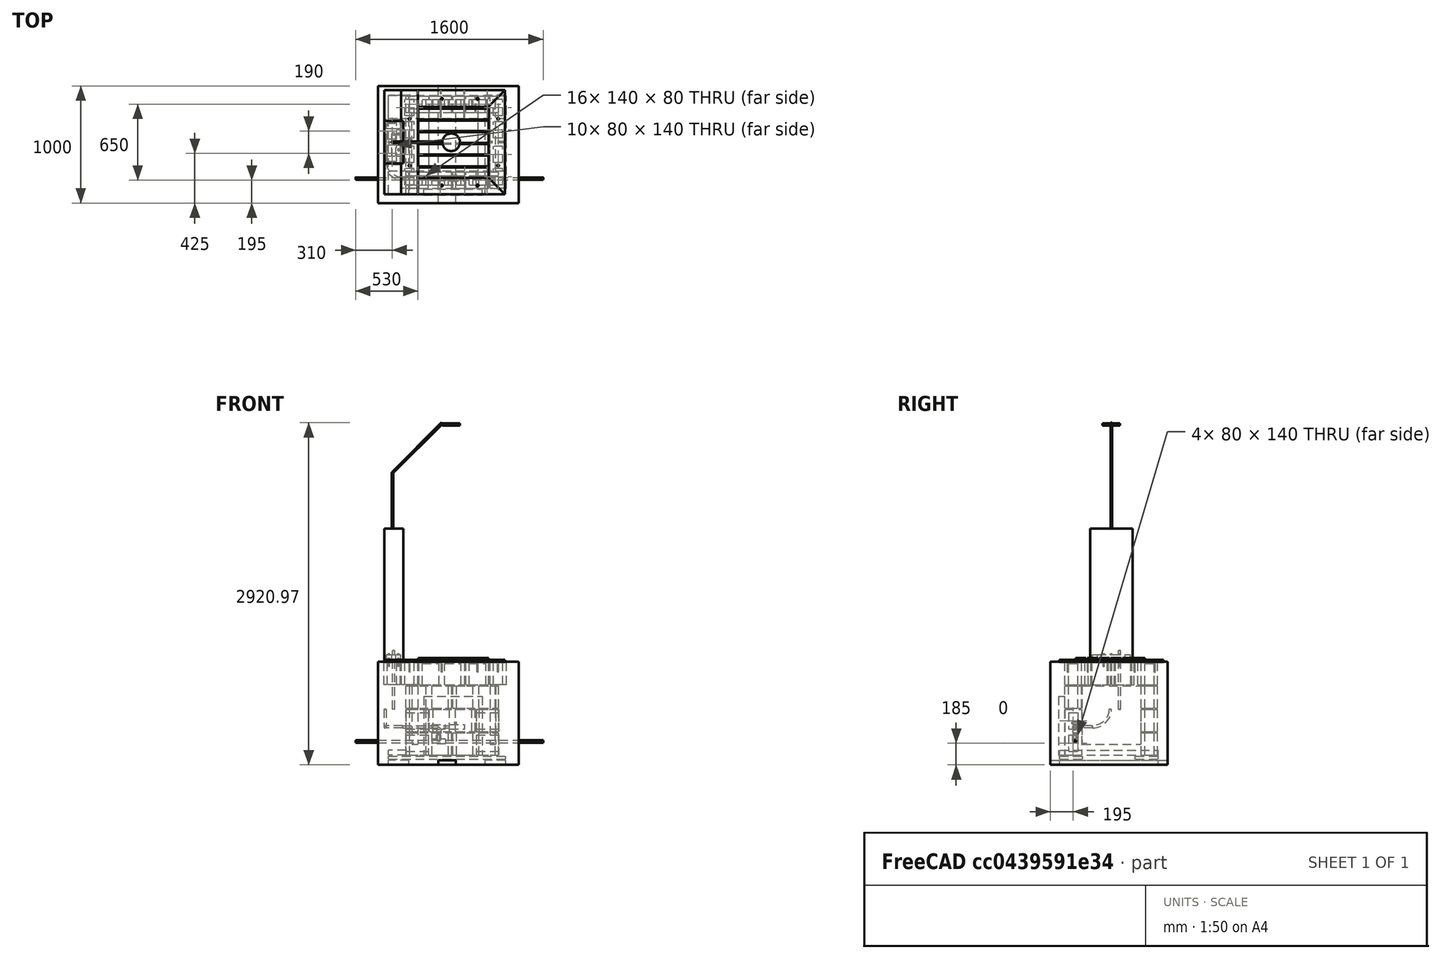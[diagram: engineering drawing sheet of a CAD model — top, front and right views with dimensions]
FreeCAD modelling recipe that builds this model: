
FCSTD DOCUMENT  (FreeCAD 0.18.3R)
Label: douchesokkel v2
License: All rights reserved
LicenseURL: http://en.wikipedia.org/wiki/All_rights_reserved
objects: Part::Box×89, Part::Cylinder×34, Part::MultiFuse×24, Part::Cut×20, Part::Compound×13, Part::Chamfer×3, Part::Torus×2
note: 185 computed .brp shape members not serialized (recipe doc carries the construction recipe); baked Part::Feature solids carry a one-line shape summary decoded from their .brp

FEATURE [Part::Box] Box  label="douchesokkel"
  AttacherType = Attacher::AttachEngine3D
  Height = 1120
  Length = 160
  Placement = pos=(45,10,21) rot=(0,0,1;0rad)
  Width = 360
FEATURE [Part::Cylinder] Cylinder  label="douchebuis"
  Angle = 360
  AttacherType = Attacher::AttachEngine3D
  Height = 480
  Placement = pos=(115,190,1141) rot=(0,0,1;0rad)
  Radius = 7
FEATURE [Part::Cylinder] Cylinder001  label="douchebuis001"
  Angle = 360
  AttacherType = Attacher::AttachEngine3D
  Height = 594
  Placement = pos=(115,190,1621) rot=(0,1,0;0.785398rad)
  Radius = 7
FEATURE [Part::Cylinder] Cylinder002  label="douchekop"
  Angle = 360
  AttacherType = Attacher::AttachEngine3D
  Height = 20
  Placement = pos=(615,190,2021) rot=(0,0,1;0rad)
  Radius = 75
FEATURE [Part::Box] Box001  label="put"
  AttacherType = Attacher::AttachEngine3D
  Height = 880
  Length = 1200
  Placement = pos=(-10,-330,-875) rot=(0,0,1;0rad)
  Width = 1000
FEATURE [Part::Cylinder] Cylinder003  label="Cylinder"
  Angle = 360
  AttacherType = Attacher::AttachEngine3D
  Height = 116
  Radius = 20
FEATURE [Part::Cylinder] Cylinder004  label="Cylinder001"
  Angle = 360
  AttacherType = Attacher::AttachEngine3D
  Height = 55
  Placement = pos=(0,0,58) rot=(0,1,0;1.5708rad)
  Radius = 20
FEATURE [Part::MultiFuse] Fusion  label="T-stuk"
  Placement = pos=(450,-120,-550) rot=(0,1,0;1.5708rad)
  Shapes = -> [Cylinder004,Cylinder003]
FEATURE [Part::Cylinder] Cylinder005  label="Cylinder002"
  Angle = 360
  AttacherType = Attacher::AttachEngine3D
  Height = 55
  Placement = pos=(0,0,58) rot=(0,1,0;1.5708rad)
  Radius = 20
FEATURE [Part::Cylinder] Cylinder006  label="Cylinder003"
  Angle = 360
  AttacherType = Attacher::AttachEngine3D
  Height = 116
  Radius = 20
FEATURE [Part::MultiFuse] Fusion001  label="T-stuk001"
  Placement = pos=(566,-120,-675) rot=(0,-1,0;1.5708rad)
  Shapes = -> [Cylinder005,Cylinder006]
FEATURE [Part::Cylinder] Cylinder007  label="Cylinder004"
  Angle = 360
  AttacherType = Attacher::AttachEngine3D
  Height = 130
  Placement = pos=(0,0,0) rot=(0,1,0;1.5708rad)
  Radius = 20
FEATURE [Part::Box] Box002  label="Cube"
  AttacherType = Attacher::AttachEngine3D
  Height = 15
  Length = 15
  Placement = pos=(46,-25,25) rot=(0,0,1;0rad)
  Width = 58
FEATURE [Part::Cylinder] Cylinder008  label="tyleen huis-yurt"
  Angle = 360
  AttacherType = Attacher::AttachEngine3D
  Height = 1600
  Placement = pos=(-200,-120,-675) rot=(0,1,0;1.5708rad)
  Radius = 10
FEATURE [Part::MultiFuse] Fusion002  label="kraan"
  Placement = pos=(600,-120,-550) rot=(0,0,1;0rad)
  Shapes = -> [Cylinder007,Box002]
FEATURE [Part::Cylinder] Cylinder009  label="Cylinder006"
  Angle = 360
  AttacherType = Attacher::AttachEngine3D
  Height = 400
  Placement = pos=(200,-100,-550) rot=(0,1,0;1.5708rad)
  Radius = 10
FEATURE [Part::Torus] Torus
  Angle1 = 180
  Angle2 = 180
  Angle3 = 90
  AttacherType = Attacher::AttachEngine3D
  Placement = pos=(200,50,-550) rot=(0,0,1;3.14159rad)
  Radius1 = 150
  Radius2 = 10
FEATURE [Part::Torus] Torus001
  Angle1 = 180
  Angle2 = 180
  Angle3 = 90
  AttacherType = Attacher::AttachEngine3D
  Placement = pos=(50,50,-400) rot=(0,1,0;1.5708rad)
  Radius1 = 150
  Radius2 = 10
FEATURE [Part::Cylinder] Cylinder010  label="Cylinder005"
  Angle = 360
  AttacherType = Attacher::AttachEngine3D
  Height = 500
  Placement = pos=(125,280,-400) rot=(0,0,1;0rad)
  Radius = 10
FEATURE [Part::Compound] Compound  label="tyleen douche"
  Links = -> [Cylinder009,Torus,Torus001,Cylinder010]
  Placement = pos=(0,-20,0) rot=(0,0,1;0rad)
FEATURE [Part::Cylinder] Cylinder011  label="tyleen"
  Angle = 360
  AttacherType = Attacher::AttachEngine3D
  Height = 100
  Placement = pos=(508,-120,-675) rot=(0,1,0;0rad)
  Radius = 10
FEATURE [Part::Box] Box010  label="Cube004"
  AttacherType = Attacher::AttachEngine3D
  Height = 190
  Length = 140
  Placement = pos=(220,30,0) rot=(0,0,1;0rad)
  Width = 80
FEATURE [Part::Box] Box011  label="Cube005"
  AttacherType = Attacher::AttachEngine3D
  Height = 190
  Length = 140
  Placement = pos=(30,30,0) rot=(0,0,1;0rad)
  Width = 80
FEATURE [Part::MultiFuse] Fusion004
  Shapes = -> [Box011,Box010]
FEATURE [Part::Box] Box012  label="Cube006"
  AttacherType = Attacher::AttachEngine3D
  Height = 190
  Length = 390
  Width = 140
FEATURE [Part::Cut] Cut001  label="snelbouwsteen (2x)001"
  Base = -> Box012
  Placement = pos=(230,-205,-400) rot=(0,1,0;1.5708rad)
  Tool = -> Fusion004
FEATURE [Part::Box] Box013  label="dal (5x)001"
  AttacherType = Attacher::AttachEngine3D
  Height = 50
  Length = 500
  Placement = pos=(280,-60,-200) rot=(0,1,0;1.5708rad)
  Width = 500
FEATURE [Part::Box] Box014  label="dal (5x)002"
  AttacherType = Attacher::AttachEngine3D
  Height = 50
  Length = 500
  Placement = pos=(945,-60,-200) rot=(0,1,0;1.5708rad)
  Width = 500
FEATURE [Part::Box] Box015  label="dal (5x)003"
  AttacherType = Attacher::AttachEngine3D
  Height = 50
  Length = 500
  Placement = pos=(380,-260,-290) rot=(-1,0,0;1.5708rad)
  Width = 500
FEATURE [Part::Box] Box017  label="Cube007"
  AttacherType = Attacher::AttachEngine3D
  Height = 190
  Length = 140
  Placement = pos=(220,30,0) rot=(0,0,1;0rad)
  Width = 80
FEATURE [Part::Box] Box018  label="Cube008"
  AttacherType = Attacher::AttachEngine3D
  Height = 190
  Length = 140
  Placement = pos=(30,30,0) rot=(0,0,1;0rad)
  Width = 80
FEATURE [Part::MultiFuse] Fusion005
  Shapes = -> [Box018,Box017]
FEATURE [Part::Box] Box019  label="Cube009"
  AttacherType = Attacher::AttachEngine3D
  Height = 190
  Length = 390
  Width = 140
FEATURE [Part::Cut] Cut002  label="snelbouwsteen (2x)002"
  Base = -> Box019
  Placement = pos=(230,-205,-390) rot=(0,1,0;0rad)
  Tool = -> Fusion005
FEATURE [Part::Box] Box020  label="Cube010"
  AttacherType = Attacher::AttachEngine3D
  Height = 190
  Length = 140
  Placement = pos=(220,30,0) rot=(0,0,1;0rad)
  Width = 80
FEATURE [Part::Box] Box021  label="Cube011"
  AttacherType = Attacher::AttachEngine3D
  Height = 190
  Length = 140
  Placement = pos=(30,30,0) rot=(0,0,1;0rad)
  Width = 80
FEATURE [Part::MultiFuse] Fusion006
  Shapes = -> [Box021,Box020]
FEATURE [Part::Box] Box022  label="Cube012"
  AttacherType = Attacher::AttachEngine3D
  Height = 190
  Length = 390
  Width = 140
FEATURE [Part::Cut] Cut003  label="snelbouwsteen (2x)003"
  Base = -> Box022
  Placement = pos=(230,445,-790) rot=(0,1,0;0rad)
  Tool = -> Fusion006
FEATURE [Part::Box] Box023  label="Cube013"
  AttacherType = Attacher::AttachEngine3D
  Height = 190
  Length = 140
  Placement = pos=(30,30,0) rot=(0,0,1;0rad)
  Width = 80
FEATURE [Part::Box] Box024  label="Cube014"
  AttacherType = Attacher::AttachEngine3D
  Height = 190
  Length = 390
  Width = 140
FEATURE [Part::Box] Box025  label="Cube015"
  AttacherType = Attacher::AttachEngine3D
  Height = 190
  Length = 140
  Placement = pos=(220,30,0) rot=(0,0,1;0rad)
  Width = 80
FEATURE [Part::MultiFuse] Fusion007
  Shapes = -> [Box023,Box025]
FEATURE [Part::Cut] Cut004  label="snelbouwsteen (2x)004"
  Base = -> Box024
  Placement = pos=(230,445,-390) rot=(0,1,0;0rad)
  Tool = -> Fusion007
FEATURE [Part::Box] Box026  label="Cube016"
  AttacherType = Attacher::AttachEngine3D
  Height = 190
  Length = 140
  Placement = pos=(220,30,0) rot=(0,0,1;0rad)
  Width = 80
FEATURE [Part::Box] Box027  label="Cube017"
  AttacherType = Attacher::AttachEngine3D
  Height = 190
  Length = 140
  Placement = pos=(30,30,0) rot=(0,0,1;0rad)
  Width = 80
FEATURE [Part::MultiFuse] Fusion008
  Shapes = -> [Box027,Box026]
FEATURE [Part::Box] Box028  label="Cube018"
  AttacherType = Attacher::AttachEngine3D
  Height = 190
  Length = 390
  Width = 140
FEATURE [Part::Cut] Cut005  label="snelbouwsteen (2x)005"
  Base = -> Box028
  Placement = pos=(830,-205,-400) rot=(0,1,0;1.5708rad)
  Tool = -> Fusion008
FEATURE [Part::Box] Box029  label="Cube019"
  AttacherType = Attacher::AttachEngine3D
  Height = 190
  Length = 140
  Placement = pos=(30,30,0) rot=(0,0,1;0rad)
  Width = 80
FEATURE [Part::Box] Box030  label="Cube020"
  AttacherType = Attacher::AttachEngine3D
  Height = 190
  Length = 390
  Width = 140
FEATURE [Part::Box] Box031  label="Cube021"
  AttacherType = Attacher::AttachEngine3D
  Height = 190
  Length = 140
  Placement = pos=(220,30,0) rot=(0,0,1;0rad)
  Width = 80
FEATURE [Part::MultiFuse] Fusion009
  Shapes = -> [Box029,Box031]
FEATURE [Part::Cut] Cut006  label="snelbouwsteen (2x)006"
  Base = -> Box030
  Placement = pos=(630,-205,-390) rot=(0,1,0;0rad)
  Tool = -> Fusion009
FEATURE [Part::Box] Box032  label="Cube022"
  AttacherType = Attacher::AttachEngine3D
  Height = 190
  Length = 140
  Placement = pos=(30,30,0) rot=(0,0,1;0rad)
  Width = 80
FEATURE [Part::Box] Box033  label="Cube023"
  AttacherType = Attacher::AttachEngine3D
  Height = 190
  Length = 390
  Width = 140
FEATURE [Part::Box] Box034  label="Cube024"
  AttacherType = Attacher::AttachEngine3D
  Height = 190
  Length = 140
  Placement = pos=(220,30,0) rot=(0,0,1;0rad)
  Width = 80
FEATURE [Part::MultiFuse] Fusion010
  Shapes = -> [Box032,Box034]
FEATURE [Part::Cut] Cut007  label="snelbouwsteen (2x)007"
  Base = -> Box033
  Placement = pos=(630,445,-390) rot=(0,1,0;0rad)
  Tool = -> Fusion010
FEATURE [Part::Box] Box035  label="Cube025"
  AttacherType = Attacher::AttachEngine3D
  Height = 190
  Length = 140
  Placement = pos=(220,30,0) rot=(0,0,1;0rad)
  Width = 80
FEATURE [Part::Box] Box036  label="Cube026"
  AttacherType = Attacher::AttachEngine3D
  Height = 190
  Length = 140
  Placement = pos=(30,30,0) rot=(0,0,1;0rad)
  Width = 80
FEATURE [Part::MultiFuse] Fusion011
  Shapes = -> [Box036,Box035]
FEATURE [Part::Box] Box037  label="Cube027"
  AttacherType = Attacher::AttachEngine3D
  Height = 190
  Length = 390
  Width = 140
FEATURE [Part::Cut] Cut008  label="snelbouwsteen (2x)008"
  Base = -> Box037
  Placement = pos=(630,445,-790) rot=(0,1,0;0rad)
  Tool = -> Fusion011
FEATURE [Part::Box] Box042  label="boord (5x)001"
  AttacherType = Attacher::AttachEngine3D
  Height = 25
  Length = 1000
  Placement = pos=(80,-250,-825) rot=(0,0,1;0rad)
  Width = 195
FEATURE [Part::Box] Box044  label="boord (5x)002"
  AttacherType = Attacher::AttachEngine3D
  Height = 25
  Length = 1000
  Placement = pos=(80,395,-825) rot=(0,0,1;0rad)
  Width = 195
FEATURE [Part::Box] Box046  label="balk (5x)001"
  AttacherType = Attacher::AttachEngine3D
  Height = 40
  Length = 840
  Placement = pos=(255,-250,-875) rot=(0,0,1;1.5708rad)
  Width = 175
FEATURE [Part::Box] Box047  label="balk (5x)002"
  AttacherType = Attacher::AttachEngine3D
  Height = 40
  Length = 840
  Placement = pos=(1080,-250,-875) rot=(0,0,1;1.5708rad)
  Width = 175
FEATURE [Part::Box] Box048  label="balk (5x)003"
  AttacherType = Attacher::AttachEngine3D
  Height = 40
  Length = 1000
  Placement = pos=(655,-330,-875) rot=(0,0,1;1.5708rad)
  Width = 150
FEATURE [Part::Box] Box052  label="balk (5x)005"
  AttacherType = Attacher::AttachEngine3D
  Height = 40
  Length = 840
  Placement = pos=(230,-250,-790) rot=(0,0,1;1.5708rad)
  Width = 150
FEATURE [Part::Box] Box056  label="Cube028"
  AttacherType = Attacher::AttachEngine3D
  Height = 190
  Length = 140
  Placement = pos=(220,30,0) rot=(0,0,1;0rad)
  Width = 80
FEATURE [Part::Box] Box057  label="Cube029"
  AttacherType = Attacher::AttachEngine3D
  Height = 190
  Length = 140
  Placement = pos=(30,30,0) rot=(0,0,1;0rad)
  Width = 80
FEATURE [Part::MultiFuse] Fusion012
  Shapes = -> [Box057,Box056]
FEATURE [Part::Box] Box058  label="Cube030"
  AttacherType = Attacher::AttachEngine3D
  Height = 190
  Length = 390
  Width = 140
FEATURE [Part::Cut] Cut009  label="snelbouwsteen (2x)009"
  Base = -> Box058
  Placement = pos=(180,-5,-190) rot=(0,0,1;1.5708rad)
  Tool = -> Fusion012
FEATURE [Part::Box] Box076  label="Cube048"
  AttacherType = Attacher::AttachEngine3D
  Height = 19
  Length = 600
  Width = 90
FEATURE [Part::Box] Box077  label="Cube049"
  AttacherType = Attacher::AttachEngine3D
  Height = 19
  Length = 600
  Placement = pos=(0,100,0) rot=(0,0,1;0rad)
  Width = 90
FEATURE [Part::Box] Box078  label="Cube050"
  AttacherType = Attacher::AttachEngine3D
  Height = 19
  Length = 600
  Placement = pos=(0,200,0) rot=(0,0,1;0rad)
  Width = 90
FEATURE [Part::Box] Box079  label="Cube051"
  AttacherType = Attacher::AttachEngine3D
  Height = 19
  Length = 600
  Placement = pos=(0,300,0) rot=(0,0,1;0rad)
  Width = 90
FEATURE [Part::Box] Box080  label="Cube052"
  AttacherType = Attacher::AttachEngine3D
  Height = 19
  Length = 600
  Placement = pos=(0,400,0) rot=(0,0,1;0rad)
  Width = 90
FEATURE [Part::Box] Box081  label="Cube053"
  AttacherType = Attacher::AttachEngine3D
  Height = 19
  Length = 600
  Placement = pos=(0,500,0) rot=(0,0,1;0rad)
  Width = 90
FEATURE [Part::Box] Box082  label="Cube054"
  AttacherType = Attacher::AttachEngine3D
  Height = 19
  Length = 90
  Placement = pos=(0,0,-19) rot=(0,0,1;0rad)
  Width = 600
FEATURE [Part::Box] Box083  label="Cube055"
  AttacherType = Attacher::AttachEngine3D
  Height = 19
  Length = 90
  Placement = pos=(510,0,-19) rot=(0,0,1;0rad)
  Width = 600
FEATURE [Part::MultiFuse] Fusion014  label="tuintegel 60x60"
  Placement = pos=(335,-115,19) rot=(0,0,1;0rad)
  Shapes = -> [Box083,Box077,Box076,Box082,Box079,Box078,Box081,Box080]
FEATURE [Part::Box] Box084  label="Cube056"
  AttacherType = Attacher::AttachEngine3D
  Height = 21
  Length = 743
  Placement = pos=(286,-275,0) rot=(0,0,1;0rad)
  Width = 143
FEATURE [Part::Box] Box085  label="Cube057"
  AttacherType = Attacher::AttachEngine3D
  Height = 21
  Length = 743
  Placement = pos=(286,472,0) rot=(0,0,1;0rad)
  Width = 143
FEATURE [Part::Box] Box086  label="Cube058"
  AttacherType = Attacher::AttachEngine3D
  Height = 21
  Length = 143
  Placement = pos=(143,-275,0) rot=(0,0,1;0rad)
  Width = 890
FEATURE [Part::Box] Box087  label="Cube059"
  AttacherType = Attacher::AttachEngine3D
  Height = 21
  Length = 143
  Placement = pos=(886,-275,0) rot=(0,0,1;0rad)
  Width = 890
FEATURE [Part::Box] Box092  label="Cube064"
  AttacherType = Attacher::AttachEngine3D
  Height = 21
  Length = 143
  Placement = pos=(0,-275,0) rot=(0,0,1;0rad)
  Width = 890
FEATURE [Part::Chamfer] Chamfer
  Base = -> Box084
  Edges = 1 edges r=142.9: [Edge7]
FEATURE [Part::Chamfer] Chamfer001
  Base = -> Box085
  Edges = 1 edges r=142.9: [Edge5]
FEATURE [Part::Chamfer] Chamfer002
  Base = -> Box087
  Edges = 2 edges r=142.9: [Edge1,Edge3]
FEATURE [Part::Compound] Compound002  label="plankenwerk"
  Links = -> [Chamfer002,Chamfer001,Chamfer,Box092,Box086]
  Placement = pos=(45,20,0) rot=(0,0,1;0rad)
FEATURE [Part::Box] Box095  label="Cube067"
  AttacherType = Attacher::AttachEngine3D
  Height = 190
  Length = 140
  Placement = pos=(30,30,0) rot=(0,0,1;0rad)
  Width = 80
FEATURE [Part::Box] Box096  label="Cube068"
  AttacherType = Attacher::AttachEngine3D
  Height = 190
  Length = 390
  Width = 140
FEATURE [Part::Box] Box097  label="Cube069"
  AttacherType = Attacher::AttachEngine3D
  Height = 190
  Length = 140
  Placement = pos=(220,30,0) rot=(0,0,1;0rad)
  Width = 80
FEATURE [Part::MultiFuse] Fusion015
  Shapes = -> [Box095,Box097]
FEATURE [Part::Cut] Cut010  label="snelbouwsteen (2x)010"
  Base = -> Box096
  Placement = pos=(430,445,-590) rot=(0,1,0;0rad)
  Tool = -> Fusion015
FEATURE [Part::Box] Box098  label="Cube070"
  AttacherType = Attacher::AttachEngine3D
  Height = 190
  Length = 140
  Placement = pos=(30,30,0) rot=(0,0,1;0rad)
  Width = 80
FEATURE [Part::Box] Box099  label="Cube071"
  AttacherType = Attacher::AttachEngine3D
  Height = 190
  Length = 140
  Placement = pos=(220,30,0) rot=(0,0,1;0rad)
  Width = 80
FEATURE [Part::MultiFuse] Fusion016
  Shapes = -> [Box098,Box099]
FEATURE [Part::Box] Box100  label="Cube072"
  AttacherType = Attacher::AttachEngine3D
  Height = 190
  Length = 195
  Width = 140
FEATURE [Part::Cut] Cut011  label="halve snelbouwsteen"
  Base = -> Box100
  Placement = pos=(230,445,-590) rot=(0,1,0;0rad)
  Tool = -> Fusion016
FEATURE [Part::Box] Box101  label="Cube073"
  AttacherType = Attacher::AttachEngine3D
  Height = 190
  Length = 140
  Placement = pos=(220,30,0) rot=(0,0,1;0rad)
  Width = 80
FEATURE [Part::Box] Box102  label="Cube074"
  AttacherType = Attacher::AttachEngine3D
  Height = 190
  Length = 140
  Placement = pos=(30,30,0) rot=(0,0,1;0rad)
  Width = 80
FEATURE [Part::MultiFuse] Fusion017
  Shapes = -> [Box102,Box101]
FEATURE [Part::Box] Box103  label="Cube075"
  AttacherType = Attacher::AttachEngine3D
  Height = 190
  Length = 195
  Width = 140
FEATURE [Part::Cut] Cut012  label="halve snelbouwsteen001"
  Base = -> Box103
  Placement = pos=(825,445,-590) rot=(0,1,0;0rad)
  Tool = -> Fusion017
FEATURE [Part::Box] Box104  label="Cube076"
  AttacherType = Attacher::AttachEngine3D
  Height = 180
  Length = 140
  Placement = pos=(30,30,0) rot=(0,0,1;0rad)
  Width = 80
FEATURE [Part::Box] Box105  label="Cube077"
  AttacherType = Attacher::AttachEngine3D
  Height = 180
  Length = 140
  Placement = pos=(220,30,0) rot=(0,0,1;0rad)
  Width = 80
FEATURE [Part::MultiFuse] Fusion018
  Shapes = -> [Box104,Box105]
FEATURE [Part::Box] Box106  label="Cube078"
  AttacherType = Attacher::AttachEngine3D
  Height = 190
  Length = 390
  Width = 140
FEATURE [Part::Cut] Cut013  label="snelbouwsteen (2x)011"
  Base = -> Box106
  Placement = pos=(340,445,-190) rot=(0,1,0;0rad)
  Tool = -> Fusion018
FEATURE [Part::Box] Box107  label="Cube079"
  AttacherType = Attacher::AttachEngine3D
  Height = 190
  Length = 390
  Width = 140
FEATURE [Part::Box] Box108  label="Cube080"
  AttacherType = Attacher::AttachEngine3D
  Height = 180
  Length = 140
  Placement = pos=(220,30,0) rot=(0,0,1;0rad)
  Width = 80
FEATURE [Part::Box] Box109  label="Cube081"
  AttacherType = Attacher::AttachEngine3D
  Height = 180
  Length = 140
  Placement = pos=(30,30,0) rot=(0,0,1;0rad)
  Width = 80
FEATURE [Part::MultiFuse] Fusion019
  Shapes = -> [Box109,Box108]
FEATURE [Part::Cut] Cut014  label="snelbouwsteen (2x)012"
  Base = -> Box107
  Placement = pos=(340,-205,-190) rot=(0,1,0;0rad)
  Tool = -> Fusion019
FEATURE [Part::Box] Box110  label="Cube082"
  AttacherType = Attacher::AttachEngine3D
  Height = 190
  Length = 390
  Width = 140
FEATURE [Part::Box] Box111  label="Cube083"
  AttacherType = Attacher::AttachEngine3D
  Height = 190
  Length = 140
  Placement = pos=(30,30,0) rot=(0,0,1;0rad)
  Width = 80
FEATURE [Part::Box] Box112  label="Cube084"
  AttacherType = Attacher::AttachEngine3D
  Height = 190
  Length = 140
  Placement = pos=(220,30,0) rot=(0,0,1;0rad)
  Width = 80
FEATURE [Part::MultiFuse] Fusion020
  Shapes = -> [Box111,Box112]
FEATURE [Part::Cut] Cut015  label="snelbouwsteen (2x)013"
  Base = -> Box110
  Placement = pos=(330,-205,-190) rot=(0,0,1;1.5708rad)
  Tool = -> Fusion020
FEATURE [Part::Box] Box113  label="Cube085"
  AttacherType = Attacher::AttachEngine3D
  Height = 190
  Length = 140
  Placement = pos=(220,30,0) rot=(0,0,1;0rad)
  Width = 80
FEATURE [Part::Box] Box114  label="Cube086"
  AttacherType = Attacher::AttachEngine3D
  Height = 190
  Length = 140
  Placement = pos=(30,30,0) rot=(0,0,1;0rad)
  Width = 80
FEATURE [Part::MultiFuse] Fusion021
  Shapes = -> [Box114,Box113]
FEATURE [Part::Box] Box115  label="Cube087"
  AttacherType = Attacher::AttachEngine3D
  Height = 190
  Length = 390
  Width = 140
FEATURE [Part::Cut] Cut016  label="snelbouwsteen (2x)014"
  Base = -> Box115
  Placement = pos=(330,195,-190) rot=(0,0,1;1.5708rad)
  Tool = -> Fusion021
FEATURE [Part::Box] Box116  label="Cube088"
  AttacherType = Attacher::AttachEngine3D
  Height = 190
  Length = 140
  Placement = pos=(220,30,0) rot=(0,0,1;0rad)
  Width = 80
FEATURE [Part::Box] Box117  label="Cube089"
  AttacherType = Attacher::AttachEngine3D
  Height = 190
  Length = 390
  Width = 140
FEATURE [Part::Box] Box118  label="Cube090"
  AttacherType = Attacher::AttachEngine3D
  Height = 190
  Length = 140
  Placement = pos=(30,30,0) rot=(0,0,1;0rad)
  Width = 80
FEATURE [Part::MultiFuse] Fusion022
  Shapes = -> [Box118,Box116]
FEATURE [Part::Cut] Cut017  label="snelbouwsteen (2x)015"
  Base = -> Box117
  Placement = pos=(1085,195,-190) rot=(0,0,1;1.5708rad)
  Tool = -> Fusion022
FEATURE [Part::Box] Box119  label="Cube091"
  AttacherType = Attacher::AttachEngine3D
  Height = 190
  Length = 140
  Placement = pos=(220,30,0) rot=(0,0,1;0rad)
  Width = 80
FEATURE [Part::Box] Box120  label="Cube092"
  AttacherType = Attacher::AttachEngine3D
  Height = 190
  Length = 140
  Placement = pos=(30,30,0) rot=(0,0,1;0rad)
  Width = 80
FEATURE [Part::MultiFuse] Fusion023
  Shapes = -> [Box120,Box119]
FEATURE [Part::Box] Box121  label="Cube093"
  AttacherType = Attacher::AttachEngine3D
  Height = 190
  Length = 390
  Width = 140
FEATURE [Part::Cut] Cut018  label="snelbouwsteen (2x)016"
  Base = -> Box121
  Placement = pos=(1085,-205,-190) rot=(0,0,1;1.5708rad)
  Tool = -> Fusion023
FEATURE [Part::Box] Box122  label="Cube094"
  AttacherType = Attacher::AttachEngine3D
  Height = 190
  Length = 195
  Width = 140
FEATURE [Part::Box] Box123  label="Cube095"
  AttacherType = Attacher::AttachEngine3D
  Height = 180
  Length = 140
  Placement = pos=(30,30,0) rot=(0,0,1;0rad)
  Width = 80
FEATURE [Part::Box] Box124  label="Cube096"
  AttacherType = Attacher::AttachEngine3D
  Height = 190
  Length = 140
  Placement = pos=(220,30,0) rot=(0,0,1;0rad)
  Width = 80
FEATURE [Part::MultiFuse] Fusion024
  Shapes = -> [Box123,Box124]
FEATURE [Part::Cut] Cut019  label="halve snelbouwsteen002"
  Base = -> Box122
  Placement = pos=(740,445,-190) rot=(0,1,0;0rad)
  Tool = -> Fusion024
FEATURE [Part::Box] Box125  label="Cube097"
  AttacherType = Attacher::AttachEngine3D
  Height = 190
  Length = 140
  Placement = pos=(220,30,0) rot=(0,0,1;0rad)
  Width = 80
FEATURE [Part::Box] Box126  label="Cube098"
  AttacherType = Attacher::AttachEngine3D
  Height = 190
  Length = 195
  Width = 140
FEATURE [Part::Box] Box127  label="Cube099"
  AttacherType = Attacher::AttachEngine3D
  Height = 180
  Length = 140
  Placement = pos=(30,30,0) rot=(0,0,1;0rad)
  Width = 80
FEATURE [Part::MultiFuse] Fusion025
  Shapes = -> [Box127,Box125]
FEATURE [Part::Cut] Cut020  label="halve snelbouwsteen003"
  Base = -> Box126
  Placement = pos=(740,-205,-190) rot=(0,1,0;0rad)
  Tool = -> Fusion025
FEATURE [Part::Box] Box128  label="Cube100"
  AttacherType = Attacher::AttachEngine3D
  Height = 44
  Length = 123
  Placement = pos=(63,28,21) rot=(0,0,1;0rad)
  Width = 44
FEATURE [Part::Box] Box129  label="Cube101"
  AttacherType = Attacher::AttachEngine3D
  Height = 44
  Length = 123
  Placement = pos=(63,308,21) rot=(0,0,1;0rad)
  Width = 44
FEATURE [Part::Box] Box130  label="Cube102"
  AttacherType = Attacher::AttachEngine3D
  Height = 44
  Length = 44
  Placement = pos=(63,72,21) rot=(0,0,1;0rad)
  Width = 236
FEATURE [Part::Box] Box131  label="Cube103"
  AttacherType = Attacher::AttachEngine3D
  Height = 44
  Length = 44
  Placement = pos=(142,72,21) rot=(0,0,1;0rad)
  Width = 236
FEATURE [Part::Cylinder] Cylinder012  label="Cylinder007"
  Angle = 360
  AttacherType = Attacher::AttachEngine3D
  Height = 6
  Radius = 8
FEATURE [Part::Cylinder] Cylinder013  label="Cylinder008"
  Angle = 360
  AttacherType = Attacher::AttachEngine3D
  Height = 100
  Placement = pos=(0,0,-100) rot=(0,0,1;0rad)
  Radius = 4
FEATURE [Part::Compound] Compound003  label="M8x10"
  Links = -> [Cylinder012,Cylinder013]
  Placement = pos=(535,-180,16) rot=(0,0,1;0rad)
FEATURE [Part::Cylinder] Cylinder014  label="Cylinder009"
  Angle = 360
  AttacherType = Attacher::AttachEngine3D
  Height = 6
  Radius = 8
FEATURE [Part::Cylinder] Cylinder015  label="Cylinder010"
  Angle = 360
  AttacherType = Attacher::AttachEngine3D
  Height = 100
  Placement = pos=(0,0,-100) rot=(0,0,1;0rad)
  Radius = 4
FEATURE [Part::Compound] Compound004  label="M8x10 (2)"
  Links = -> [Cylinder014,Cylinder015]
  Placement = pos=(840,-180,16) rot=(0,0,1;0rad)
FEATURE [Part::Cylinder] Cylinder016  label="Cylinder011"
  Angle = 360
  AttacherType = Attacher::AttachEngine3D
  Height = 6
  Radius = 8
FEATURE [Part::Cylinder] Cylinder017  label="Cylinder012"
  Angle = 360
  AttacherType = Attacher::AttachEngine3D
  Height = 100
  Placement = pos=(0,0,-100) rot=(0,0,1;0rad)
  Radius = 4
FEATURE [Part::Compound] Compound005  label="M8x10 (2)001"
  Links = -> [Cylinder016,Cylinder017]
  Placement = pos=(840,560,16) rot=(0,0,1;0rad)
FEATURE [Part::Cylinder] Cylinder018  label="Cylinder013"
  Angle = 360
  AttacherType = Attacher::AttachEngine3D
  Height = 6
  Radius = 8
FEATURE [Part::Cylinder] Cylinder019  label="Cylinder014"
  Angle = 360
  AttacherType = Attacher::AttachEngine3D
  Height = 100
  Placement = pos=(0,0,-100) rot=(0,0,1;0rad)
  Radius = 4
FEATURE [Part::Compound] Compound006  label="M8x011"
  Links = -> [Cylinder018,Cylinder019]
  Placement = pos=(535,560,16) rot=(0,0,1;0rad)
FEATURE [Part::Cylinder] Cylinder020  label="Cylinder015"
  Angle = 360
  AttacherType = Attacher::AttachEngine3D
  Height = 6
  Radius = 8
FEATURE [Part::Cylinder] Cylinder021  label="Cylinder016"
  Angle = 360
  AttacherType = Attacher::AttachEngine3D
  Height = 100
  Placement = pos=(0,0,-100) rot=(0,0,1;0rad)
  Radius = 4
FEATURE [Part::Compound] Compound007  label="M8x012"
  Links = -> [Cylinder020,Cylinder021]
  Placement = pos=(1015,390,16) rot=(0,0,1;0rad)
FEATURE [Part::Cylinder] Cylinder022  label="Cylinder017"
  Angle = 360
  AttacherType = Attacher::AttachEngine3D
  Height = 6
  Radius = 8
FEATURE [Part::Cylinder] Cylinder023  label="Cylinder018"
  Angle = 360
  AttacherType = Attacher::AttachEngine3D
  Height = 100
  Placement = pos=(0,0,-100) rot=(0,0,1;0rad)
  Radius = 4
FEATURE [Part::Compound] Compound008  label="M8x013"
  Links = -> [Cylinder022,Cylinder023]
  Placement = pos=(1015,-10,16) rot=(0,0,1;0rad)
FEATURE [Part::Cylinder] Cylinder024  label="Cylinder019"
  Angle = 360
  AttacherType = Attacher::AttachEngine3D
  Height = 6
  Radius = 8
FEATURE [Part::Cylinder] Cylinder025  label="Cylinder020"
  Angle = 360
  AttacherType = Attacher::AttachEngine3D
  Height = 100
  Placement = pos=(0,0,-100) rot=(0,0,1;0rad)
  Radius = 4
FEATURE [Part::Compound] Compound009  label="M8x014"
  Links = -> [Cylinder024,Cylinder025]
  Placement = pos=(260,390,16) rot=(0,0,1;0rad)
FEATURE [Part::Cylinder] Cylinder026  label="Cylinder021"
  Angle = 360
  AttacherType = Attacher::AttachEngine3D
  Height = 6
  Radius = 8
FEATURE [Part::Cylinder] Cylinder027  label="Cylinder022"
  Angle = 360
  AttacherType = Attacher::AttachEngine3D
  Height = 100
  Placement = pos=(0,0,-100) rot=(0,0,1;0rad)
  Radius = 4
FEATURE [Part::Compound] Compound010  label="M8x015"
  Links = -> [Cylinder026,Cylinder027]
  Placement = pos=(260,-10,16) rot=(0,0,1;0rad)
FEATURE [Part::Cylinder] Cylinder028  label="Cylinder023"
  Angle = 360
  AttacherType = Attacher::AttachEngine3D
  Height = 6
  Radius = 8
FEATURE [Part::Cylinder] Cylinder029  label="Cylinder024"
  Angle = 360
  AttacherType = Attacher::AttachEngine3D
  Height = 100
  Placement = pos=(0,0,-100) rot=(0,0,1;0rad)
  Radius = 4
FEATURE [Part::Compound] Compound011  label="M8x016"
  Links = -> [Cylinder028,Cylinder029]
  Placement = pos=(165,260,65) rot=(0,0,1;0rad)
FEATURE [Part::Cylinder] Cylinder030  label="Cylinder025"
  Angle = 360
  AttacherType = Attacher::AttachEngine3D
  Height = 6
  Radius = 8
FEATURE [Part::Cylinder] Cylinder031  label="Cylinder026"
  Angle = 360
  AttacherType = Attacher::AttachEngine3D
  Height = 100
  Placement = pos=(0,0,-100) rot=(0,0,1;0rad)
  Radius = 4
FEATURE [Part::Compound] Compound012  label="M8x017"
  Links = -> [Cylinder030,Cylinder031]
  Placement = pos=(165,125,65) rot=(0,0,1;0rad)
FEATURE [Part::Cylinder] Cylinder032  label="Cylinder027"
  Angle = 360
  AttacherType = Attacher::AttachEngine3D
  Height = 6
  Radius = 8
FEATURE [Part::Cylinder] Cylinder033  label="Cylinder028"
  Angle = 360
  AttacherType = Attacher::AttachEngine3D
  Height = 100
  Placement = pos=(0,0,-100) rot=(0,0,1;0rad)
  Radius = 4
FEATURE [Part::Compound] Compound013  label="M8x018"
  Links = -> [Cylinder032,Cylinder033]
  Placement = pos=(85,190,65) rot=(0,0,1;0rad)
